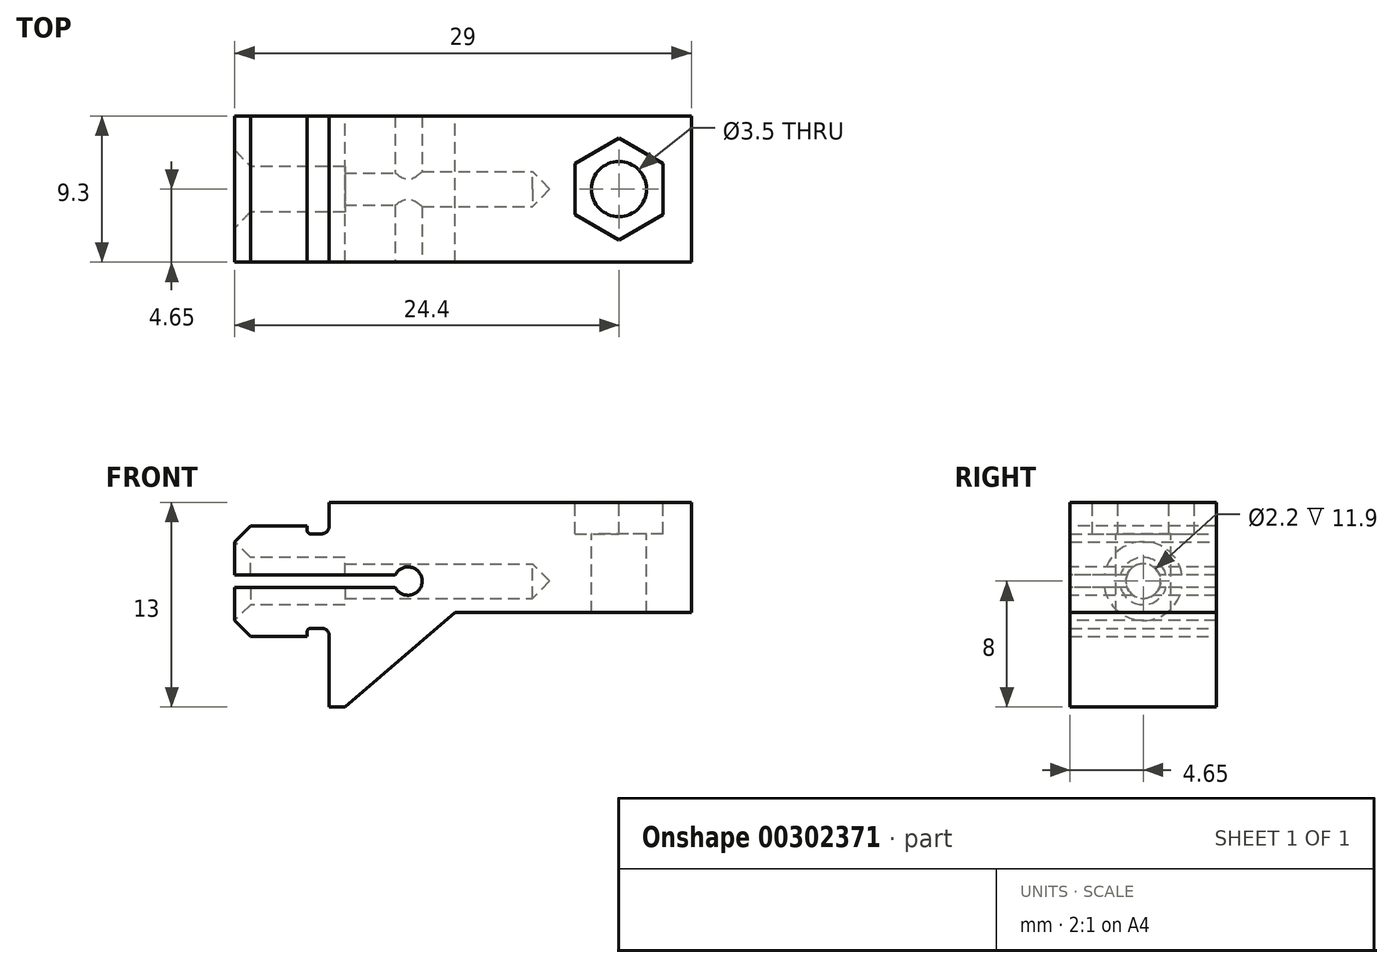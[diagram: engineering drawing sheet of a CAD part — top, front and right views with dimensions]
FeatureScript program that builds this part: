
annotation { "Feature Type Name" : "Feature", "Feature Type Description" : "" }
export const myFeature = defineFeature(function(context is Context, id is Id, definition is map)
    precondition{}
    {
        {
            var Q0;
            Q0=qCreatedBy(makeId("Front.planeOp"),FACE);
            var sketch = newSketch(context, id + "F0", { "sketchPlane" : qUnion([Q0])});
            skLineSegment(sketch, "E0", {"start": v(0, 0) * mm, "end": v(23, 0) * mm});
            skLineSegment(sketch, "E1", {"start": v(23, 0) * mm, "end": v(23, -7) * mm});
            skLineSegment(sketch, "E2", {"start": v(23, -7) * mm, "end": v(8, -7) * mm});
            skLineSegment(sketch, "E3", {"start": v(8, -7) * mm, "end": v(1, -13) * mm});
            skLineSegment(sketch, "E4", {"start": v(1, -13) * mm, "end": v(0, -13) * mm});
            skLineSegment(sketch, "E5", {"start": v(0, -13) * mm, "end": v(0, -8.5) * mm});
            skLineSegment(sketch, "E6", {"start": v(0, -8.5) * mm, "end": v(-6, -8.5) * mm});
            skLineSegment(sketch, "E7", {"start": v(-6, -8.5) * mm, "end": v(-6, -1.5) * mm});
            skLineSegment(sketch, "E8", {"start": v(-6, -1.5) * mm, "end": v(0, -1.5) * mm});
            skLineSegment(sketch, "E9", {"start": v(0, 0) * mm, "end": v(0, -1.5) * mm});
            skLineSegment(sketch, "E10", {"start": v(0, -1.5) * mm, "end": v(0, -2) * mm});
            skLineSegment(sketch, "E11", {"start": v(0, -2) * mm, "end": v(-1.4, -2) * mm});
            skLineSegment(sketch, "E12", {"start": v(-1.4, -2) * mm, "end": v(-1.4, -1.5) * mm});
            skLineSegment(sketch, "E13", {"start": v(0, -8.5) * mm, "end": v(0, -8) * mm});
            skLineSegment(sketch, "E14", {"start": v(0, -8) * mm, "end": v(-1.4, -8) * mm});
            skLineSegment(sketch, "E15", {"start": v(-1.4, -8) * mm, "end": v(-1.4, -8.5) * mm});
            skSolve(sketch);
        }
        {
            var Q0;
            Q0=makeQuery(id+"F0.imprint","IMPRINT",FACE,{"disambiguationData":[TD([[makeQuery(id+"F0.imprint","IMPRINT",EDGE,{"derivedFrom":sQuery(id+"F0.wireOp",EDGE,"E0")}),-1.0]])]});
            extrude(context, id + "F1", {"entities" : qUnion([Q0]), "endBound" : BoundingType.SYMMETRIC, "depth" : 9.3 * mm});
        }
        {
            var Q0;
            Q0=makeQuery(id+"F1.opExtrude","SWEPT_FACE",FACE,{"disambiguationData":[OSD([sQuery(id+"F0.wireOp",EDGE,"E0")])]});
            var sketch = newSketch(context, id + "F2", { "sketchPlane" : qUnion([Q0])});
            skCircle(sketch, "E16", {"center": v(18.4, 0) * mm, "radius": 1.75 * mm});
            skCircle(sketch, "E17.cCircle", {"center": v(18.4, 0) * mm, "radius": 2.8 * mm, "construction": true});
            skLineSegment(sketch, "E17.0", {"start": v(15.6, 1.62) * mm, "end": v(18.4, 3.23) * mm});
            skLineSegment(sketch, "E17.1", {"start": v(18.4, 3.23) * mm, "end": v(21.2, 1.62) * mm});
            skLineSegment(sketch, "E17.2", {"start": v(21.2, 1.62) * mm, "end": v(21.2, -1.62) * mm});
            skLineSegment(sketch, "E17.3", {"start": v(21.2, -1.62) * mm, "end": v(18.4, -3.23) * mm});
            skLineSegment(sketch, "E17.4", {"start": v(18.4, -3.23) * mm, "end": v(15.6, -1.62) * mm});
            skLineSegment(sketch, "E17.5", {"start": v(15.6, -1.62) * mm, "end": v(15.6, 1.62) * mm});
            skPoint(sketch, "E17.0.midPoint", {"position": v(17, 2.42) * mm});
            skSolve(sketch);
        }
        {
            var Q0;
            Q0=makeQuery(id+"F2.imprint","IMPRINT",FACE,{"disambiguationData":[TD([[makeQuery(id+"F2.imprint","IMPRINT",EDGE,{"derivedFrom":sQuery(id+"F2.wireOp",EDGE,"E16")}),1.0]])]});
            extrude(context, id + "F3", {"entities" : qUnion([Q0]), "operationType" : NewBodyOperationType.REMOVE, "endBound" : BoundingType.THROUGH_ALL, "oppositeDirection" : true, "depth" : 25 * mm});
        }
        {
            var Q0;
            Q0=makeQuery(id+"F2.imprint","IMPRINT",FACE,{"disambiguationData":[TD([[makeQuery(id+"F2.imprint","IMPRINT",EDGE,{"derivedFrom":sQuery(id+"F2.wireOp",EDGE,"E16")}),-1.0]])]});
            extrude(context, id + "F4", {"entities" : qUnion([Q0]), "operationType" : NewBodyOperationType.REMOVE, "oppositeDirection" : true, "depth" : 2 * mm});
        }
        {
            var Q0;
            Q0=qCreatedBy(makeId("Front.planeOp"),FACE);
            var sketch = newSketch(context, id + "F5", { "sketchPlane" : qUnion([Q0])});
            skLineSegment(sketch, "E18", {"start": v(-6, -5) * mm, "end": v(14, -5) * mm});
            skLineSegment(sketch, "E19", {"start": v(14, -5) * mm, "end": v(12.9, -3.9) * mm});
            skLineSegment(sketch, "E20", {"start": v(12.9, -3.9) * mm, "end": v(-4.6, -3.9) * mm});
            skLineSegment(sketch, "E21", {"start": v(-4.6, -3.9) * mm, "end": v(-6, -2.5) * mm});
            skLineSegment(sketch, "E22", {"start": v(-6, -2.5) * mm, "end": v(-6, -5) * mm});
            skLineSegment(sketch, "E23", {"start": v(14, -5) * mm, "end": v(30.8, -5) * mm, "construction": true});
            skLineSegment(sketch, "E24.0", {"start": v(-6, -8.5) * mm, "end": v(-6, -1.5) * mm});
            skSolve(sketch);
        }
        {
            var Q0;
            {var subQ1=sQuery(id+"F5.wireOp",EDGE,"E18");Q0=makeQuery(id+"F5.imprint","IMPRINT",FACE,{"disambiguationData":[TD([[makeQuery(id+"F5.imprint","IMPRINT",EDGE,{"derivedFrom":subQ1}),1.0]])]});}
            var Q1;
            Q1=sQuery(id+"F5.wireOp",EDGE,"E23");
            revolve(context, id + "F6", {"operationType" : NewBodyOperationType.REMOVE, "entities" : qUnion([Q0]), "axis" : qUnion([Q1]), "revolveType" : RevolveType.FULL, "oppositeDirection" : true});
        }
        {
            var Q0;
            Q0=qCreatedBy(makeId("Front.planeOp"),FACE);
            var sketch = newSketch(context, id + "F7", { "sketchPlane" : qUnion([Q0])});
            skLineSegment(sketch, "E25.0", {"start": v(14, -5) * mm, "end": v(30.8, -5) * mm});
            skCircle(sketch, "E26", {"center": v(5, -5) * mm, "radius": 0.9 * mm});
            skLineSegment(sketch, "E27.0", {"start": v(-6, -8.5) * mm, "end": v(-6, -1.5) * mm});
            skLineSegment(sketch, "E28", {"start": v(4.2, -4.6) * mm, "end": v(-6, -4.6) * mm});
            skLineSegment(sketch, "E29", {"start": v(4.2, -5.4) * mm, "end": v(-6, -5.4) * mm});
            skSolve(sketch);
        }
        {
            var Q0;
            Q0 = qSketchRegion(id + "F7", true);
            extrude(context, id + "F8", {"entities" : qUnion([Q0]), "operationType" : NewBodyOperationType.REMOVE, "endBound" : BoundingType.SYMMETRIC, "oppositeDirection" : true, "depth" : 25 * mm});
        }
        {
            var Q0;
            Q0=makeQuery(id+"F1.opExtrude","SWEPT_EDGE",EDGE,{"disambiguationData":[OSD([sQuery(id+"F0.wireOp",EDGE,"E6"),sQuery(id+"F0.wireOp",EDGE,"E7")])]});
            var Q1;
            Q1=makeQuery(id+"F1.opExtrude","SWEPT_EDGE",EDGE,{"disambiguationData":[OSD([sQuery(id+"F0.wireOp",EDGE,"E7"),sQuery(id+"F0.wireOp",EDGE,"E8")])]});
            chamfer(context, id + "F9", {"entities" : qUnion([Q0, Q1]), "width" : 1 * mm, "tangentPropagation" : true});
        }
        {
            var Q0;
            Q0=makeQuery(id+"F1.opExtrude","SWEPT_EDGE",EDGE,{"disambiguationData":[OSD([sQuery(id+"F0.wireOp",EDGE,"E10"),sQuery(id+"F0.wireOp",EDGE,"E11")])]});
            var Q1;
            Q1=makeQuery(id+"F1.opExtrude","SWEPT_EDGE",EDGE,{"disambiguationData":[OSD([sQuery(id+"F0.wireOp",EDGE,"E13"),sQuery(id+"F0.wireOp",EDGE,"E14")])]});
            fillet(context, id + "F10", {"entities" : qUnion([Q0, Q1]), "radius" : .5 * mm, "tangentPropagation" : true, "allowEdgeOverflow" : false});
        }
        {
            var Q0;
            Q0=makeQuery(id+"F1.opExtrude","SWEPT_EDGE",EDGE,{"disambiguationData":[OSD([sQuery(id+"F0.wireOp",EDGE,"E11"),sQuery(id+"F0.wireOp",EDGE,"E12")])]});
            var Q1;
            Q1=makeQuery(id+"F1.opExtrude","SWEPT_EDGE",EDGE,{"disambiguationData":[OSD([sQuery(id+"F0.wireOp",EDGE,"E14"),sQuery(id+"F0.wireOp",EDGE,"E15")])]});
            fillet(context, id + "F11", {"entities" : qUnion([Q0, Q1]), "radius" : .2 * mm, "tangentPropagation" : true, "allowEdgeOverflow" : false});
        }
        {
            var Q0;
            Q0=qCreatedBy(makeId("Front.planeOp"),FACE);
            var sketch = newSketch(context, id + "F12", { "sketchPlane" : qUnion([Q0])});
            skLineSegment(sketch, "E30.0", {"start": v(-6, -5) * mm, "end": v(14, -5) * mm});
            skLineSegment(sketch, "E31.bottom", {"start": v(-6, -5) * mm, "end": v(1, -5) * mm});
            skLineSegment(sketch, "E31.top", {"start": v(-6, -3.5) * mm, "end": v(1, -3.5) * mm});
            skLineSegment(sketch, "E31.left", {"start": v(-6, -5) * mm, "end": v(-6, -3.5) * mm});
            skLineSegment(sketch, "E31.right", {"start": v(1, -5) * mm, "end": v(1, -3.5) * mm});
            skSolve(sketch);
        }
        {
            var Q0;
            Q0 = qSketchRegion(id + "F12", true);
            var Q1;
            Q1=sQuery(id+"F12.wireOp",EDGE,"E30.0");
            revolve(context, id + "F13", {"operationType" : NewBodyOperationType.REMOVE, "entities" : qUnion([Q0]), "axis" : qUnion([Q1]), "revolveType" : RevolveType.FULL});
        }
    });
